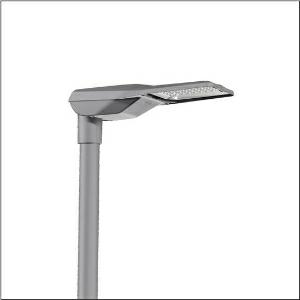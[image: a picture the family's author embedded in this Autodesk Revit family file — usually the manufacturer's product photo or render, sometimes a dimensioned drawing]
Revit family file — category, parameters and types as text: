
# Revit family: streetlight_sl_21_iq_mini___st1_5a_5xe2p41g08gb_fe87
name_source: partatom
category: Lighting Fixtures
units: mm (PartAtom-declared; Revit-internal decimal feet)

## family parameters
Cut with Voids When Loaded = No
Host = Face
Light Source = No
Part Type = Normal
Room Calculation Point = No
Round Connector Dimension = Use Diameter
Shared = No

## types (1)
- --- (1 x LED, 5810 lm, 37.1 W, 4000K)
    Apparent Load = 37 VA
    CIE Flux Codes = 22 53 95 100 100
    Color Rendering = 70
    Color Temperature = 4000K
    Default Elevation = 1800 mm
    Description = Streetlight SL 21 iQ mini, mast luminaire, primary light control with lens, of PMMA, primary optical cover: cover, of toughened safety glass, transparent, light distribution: ST1.5a, light emission: direct distribution, primary light characteristic: asymmetric, installation type: post-top, side-entry, LED, High Power LED, rated luminous flux: 5.810lm, luminous efficacy: 157lm/W, light colour: 740, colour temperature: 4000K, control gear: iQ Street-Remote, control: Street-Remote, Auto-Match, Temp-Guard, Lumen-Switch, Night-Set, Smart-Wire, Light-Fading, Desk-Remote (wireless, voltage-free reading and setting of iQ features in the workshop via application-optimized NFC function/RFID function), optimised constant luminous flux control (CLO 2.0), pre-setting: linear dimming characteristic, mains connection: 220..240V, AC, 50/60Hz, start of lifetime: 37W, end of service life: 39W, reduction: 18W, luminaire housing, of diecast aluminium, powder-coated, SITECO metallic grey (DB 702S), corrosivity category C5 high according to DIN EN ISO 12944, please order mast flange separately, inclination adjustable: 0°, 5°, 10°, 15°, sealing non-destructively replaceable, multi-level sealing system, length: 628mm, width: 235mm, height: 110mm, mast flange for spigot size: 42mm (side-entry): 5XC10008XM4, 60/48mm (side-entry/post-top): 5XC10108XM2, 76/60mm (side-entry/post-top): 5XC10108XM1, mounting height: 4..8m, protection rating (complete): IP66, insulation class (complete): insulation class II (safety insulation), certification: CE, ENEC, ENEC+, VDE, impact resistance: IK10, permissible operating ambient temperature for outdoor applications: -40..+50°C, standard-compliant lighting for roads and squares, packaging unit: 1 piece

Light Distribution: ST1.5a
    Height = 110 mm
    Lamp = 1 x LED
    Lamp Light Flux = 5810 lm
    Lamp Power = 37.1 W
    Lamp count = 1
    Length = 625 mm
    Luminous efficacy = 157 lm/W
    Manufacturer = Siteco
    ModVariant = No
    Model = 5XE2P41G08GB
    Number of Poles = 1
    OnlyDefault = Yes
    Power Factor = 1
    Product Name = Streetlight SL 21 iQ mini | ST1.5a
    Product group = mast luminaire | pylon top
    ProductGroupID = 6100
    Protection Class = Protection class II
    Protection Degree = IP 66
    RLX_Detail_Level = 1
    RLX_Emergency_Light_Flux = 0 lm
    RLX_Emergency_Type = 0
    RLX_Emergency_Type_DB = No
    RlxData = <blob elided: 29929 chars, md5=2fb09e45>
    Socket = socket
    Standby Power = 0 W
    System Light Flux = 5810 lm
    System Power = 37 W
    Type Comments = factory setting: luminous flux: 100 % | dim-lin: 254 | 385 mA
    Type Image = l_1003519.jpg
    URL = http://relux.com
    VarID = @adj_175237
    Voltage = 0 V
    Weight = 0.00 kg
    Width = 234 mm

## geometry (parser evidence)
native form markers: Blend x4, Sweep x11
no freeform markers — native parametric forms only
